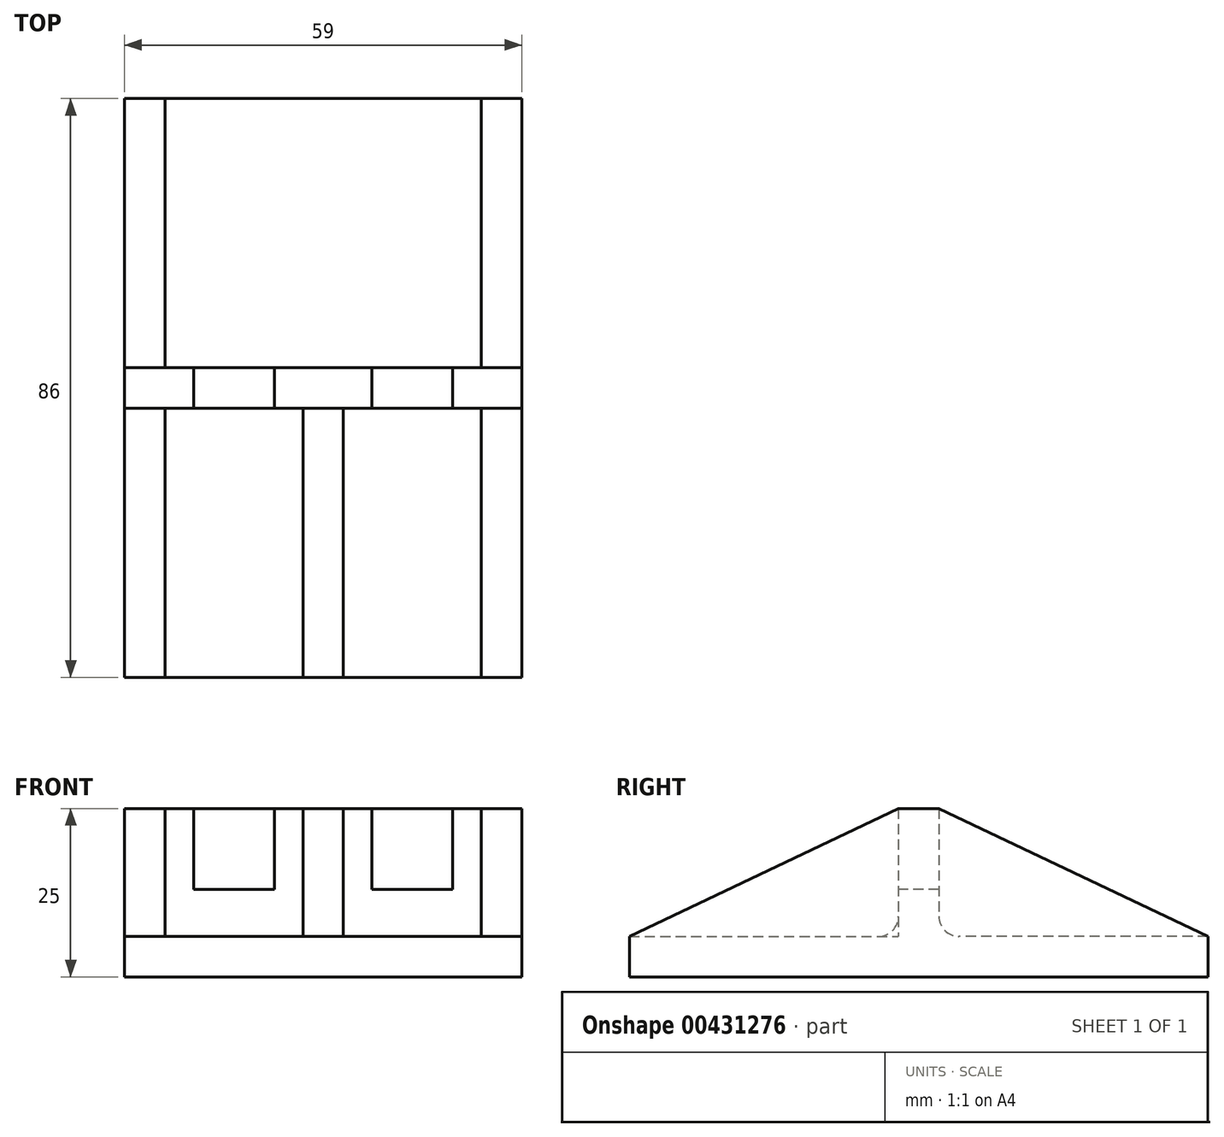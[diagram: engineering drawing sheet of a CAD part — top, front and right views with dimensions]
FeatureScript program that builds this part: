
annotation { "Feature Type Name" : "Feature", "Feature Type Description" : "" }
export const myFeature = defineFeature(function(context is Context, id is Id, definition is map)
    precondition{}
    {
        {
            var Q0;
            Q0=qCreatedBy(makeId("Top.planeOp"),FACE);
            var sketch = newSketch(context, id + "F0", { "sketchPlane" : qUnion([Q0])});
            skLineSegment(sketch, "E0.bottom", {"start": v(-29.5, 43) * mm, "end": v(29.5, 43) * mm});
            skLineSegment(sketch, "E0.top", {"start": v(-29.5, -43) * mm, "end": v(29.5, -43) * mm});
            skLineSegment(sketch, "E0.left", {"start": v(-29.5, 43) * mm, "end": v(-29.5, -43) * mm});
            skLineSegment(sketch, "E0.right", {"start": v(29.5, 43) * mm, "end": v(29.5, -43) * mm});
            skSolve(sketch);
        }
        {
            var Q0;
            Q0=makeQuery(id+"F0.imprint","IMPRINT",FACE,{"disambiguationData":[TD([[makeQuery(id+"F0.imprint","IMPRINT",EDGE,{"derivedFrom":sQuery(id+"F0.wireOp",EDGE,"E0.bottom")}),-1.0]])]});
            extrude(context, id + "F1", {"entities" : qUnion([Q0]), "depth" : 6 * mm});
        }
        {
            var Q0;
            Q0=makeQuery(id+"F1.opExtrude","CAP_FACE",FACE,{"disambiguationData":[OSD([sQuery(id+"F0.wireOp",EDGE,"E0.bottom"),sQuery(id+"F0.wireOp",EDGE,"E0.top"),sQuery(id+"F0.wireOp",EDGE,"E0.left"),sQuery(id+"F0.wireOp",EDGE,"E0.right")])],"isStart":false});
            var sketch = newSketch(context, id + "F2", { "sketchPlane" : qUnion([Q0])});
            skLineSegment(sketch, "E1.bottom", {"start": v(-29.5, 43) * mm, "end": v(-23.5, 43) * mm});
            skLineSegment(sketch, "E1.left", {"start": v(-29.5, 43) * mm, "end": v(-29.5, -43) * mm});
            skLineSegment(sketch, "E1.right", {"start": v(-23.5, 43) * mm, "end": v(-23.5, 3) * mm});
            skLineSegment(sketch, "E2.bottom", {"start": v(-23.5, 3) * mm, "end": v(23.5, 3) * mm});
            skLineSegment(sketch, "E2.top", {"start": v(-23.5, -3) * mm, "end": v(-3, -3) * mm});
            skLineSegment(sketch, "E2.right", {"start": v(29.5, 43) * mm, "end": v(29.5, -43) * mm});
            skLineSegment(sketch, "E3.bottom", {"start": v(-29.5, -43) * mm, "end": v(-23.5, -43) * mm});
            skLineSegment(sketch, "E3.right", {"start": v(-23.5, -43) * mm, "end": v(-23.5, -3) * mm});
            skLineSegment(sketch, "E4.bottom", {"start": v(29.5, -43) * mm, "end": v(23.5, -43) * mm});
            skLineSegment(sketch, "E4.right", {"start": v(23.5, -43) * mm, "end": v(23.5, -3) * mm});
            skLineSegment(sketch, "E5.bottom", {"start": v(29.5, 43) * mm, "end": v(23.5, 43) * mm});
            skLineSegment(sketch, "E5.right", {"start": v(23.5, 43) * mm, "end": v(23.5, 3) * mm});
            skLineSegment(sketch, "E6.bottom", {"start": v(3, -43) * mm, "end": v(-3, -43) * mm});
            skLineSegment(sketch, "E6.left", {"start": v(3, -43) * mm, "end": v(3, -3) * mm});
            skLineSegment(sketch, "E6.right", {"start": v(-3, -43) * mm, "end": v(-3, -3) * mm});
            skLineSegment(sketch, "E7.trimOffspring", {"start": v(3, -3) * mm, "end": v(23.5, -3) * mm});
            skPoint(sketch, "E8.orphan", {"position": v(29.5, -3) * mm});
            skSolve(sketch);
        }
        {
            var Q0;
            Q0=makeQuery(id+"F2.imprint","IMPRINT",FACE,{"disambiguationData":[TD([[makeQuery(id+"F2.imprint","IMPRINT",EDGE,{"derivedFrom":sQuery(id+"F2.wireOp",EDGE,"E1.bottom")}),-1.0]])]});
            extrude(context, id + "F3", {"entities" : qUnion([Q0]), "operationType" : NewBodyOperationType.ADD, "depth" : 19 * mm});
        }
        {
            var Q0;
            Q0=makeQuery(id+"F3.boolean.opBoolean","MERGE",FACE,{"derivedFrom":[makeQuery(id+"F1.opExtrude","SWEPT_FACE",FACE,{"disambiguationData":[OSD([sQuery(id+"F0.wireOp",EDGE,"E0.right")])]}),makeQuery(id+"F3.opExtrude","SWEPT_FACE",FACE,{"disambiguationData":[OSD([sQuery(id+"F2.wireOp",EDGE,"E2.right")])]})]});
            var sketch = newSketch(context, id + "F4", { "sketchPlane" : qUnion([Q0])});
            skLineSegment(sketch, "E9", {"start": v(-43, 6) * mm, "end": v(-3, 25) * mm});
            skLineSegment(sketch, "E10", {"start": v(-3, 25) * mm, "end": v(-43, 25) * mm});
            skLineSegment(sketch, "E11", {"start": v(-43, 25) * mm, "end": v(-43, 6) * mm});
            skLineSegment(sketch, "E12", {"start": v(43, 6) * mm, "end": v(3, 25) * mm});
            skLineSegment(sketch, "E13", {"start": v(3, 25) * mm, "end": v(43, 25) * mm});
            skLineSegment(sketch, "E14", {"start": v(43, 25) * mm, "end": v(43, 6) * mm});
            skSolve(sketch);
        }
        {
            var Q0;
            Q0=makeQuery(id+"F4.imprint","IMPRINT",FACE,{"disambiguationData":[TD([[makeQuery(id+"F4.imprint","IMPRINT",EDGE,{"derivedFrom":sQuery(id+"F4.wireOp",EDGE,"E9")}),1.0]])]});
            var Q1;
            Q1=makeQuery(id+"F4.imprint","IMPRINT",FACE,{"disambiguationData":[TD([[makeQuery(id+"F4.imprint","IMPRINT",EDGE,{"derivedFrom":sQuery(id+"F4.wireOp",EDGE,"E12")}),-1.0]])]});
            extrude(context, id + "F5", {"entities" : qUnion([Q0, Q1]), "operationType" : NewBodyOperationType.REMOVE, "endBound" : BoundingType.THROUGH_ALL, "oppositeDirection" : true, "depth" : 25 * mm});
        }
        {
            var Q0;
            Q0=makeQuery(id+"F3.opExtrude","SWEPT_FACE",FACE,{"disambiguationData":[OSD([sQuery(id+"F2.wireOp",EDGE,"E2.top")])]});
            var sketch = newSketch(context, id + "F6", { "sketchPlane" : qUnion([Q0])});
            skLineSegment(sketch, "E15.bottom", {"start": v(-19.25, 25) * mm, "end": v(-7.25, 25) * mm});
            skLineSegment(sketch, "E15.top", {"start": v(-19.25, 13) * mm, "end": v(-7.25, 13) * mm});
            skLineSegment(sketch, "E15.left", {"start": v(-19.25, 25) * mm, "end": v(-19.25, 13) * mm});
            skLineSegment(sketch, "E15.right", {"start": v(-7.25, 25) * mm, "end": v(-7.25, 13) * mm});
            skLineSegment(sketch, "E16.bottom", {"start": v(7.25, 25) * mm, "end": v(19.25, 25) * mm});
            skLineSegment(sketch, "E16.top", {"start": v(7.25, 13) * mm, "end": v(19.25, 13) * mm});
            skLineSegment(sketch, "E16.left", {"start": v(7.25, 25) * mm, "end": v(7.25, 13) * mm});
            skLineSegment(sketch, "E16.right", {"start": v(19.25, 25) * mm, "end": v(19.25, 13) * mm});
            skSolve(sketch);
        }
        {
            var Q0;
            Q0=makeQuery(id+"F6.imprint","IMPRINT",FACE,{"disambiguationData":[TD([[makeQuery(id+"F6.imprint","IMPRINT",EDGE,{"derivedFrom":sQuery(id+"F6.wireOp",EDGE,"E15.bottom")}),-1.0]])]});
            var Q1;
            Q1=makeQuery(id+"F6.imprint","IMPRINT",FACE,{"disambiguationData":[TD([[makeQuery(id+"F6.imprint","IMPRINT",EDGE,{"derivedFrom":sQuery(id+"F6.wireOp",EDGE,"E16.bottom")}),-1.0]])]});
            extrude(context, id + "F7", {"entities" : qUnion([Q0, Q1]), "oppositeDirection" : true, "depth" : 6 * mm});
        }
        {
            var Q0;
            Q0=makeQuery(id+"F3.opExtrude","CAP_EDGE",EDGE,{"disambiguationData":[OSD([sQuery(id+"F2.wireOp",EDGE,"E2.top")])],"isStart":true});
            var Q1;
            Q1=makeQuery(id+"F3.opExtrude","CAP_EDGE",EDGE,{"disambiguationData":[OSD([sQuery(id+"F2.wireOp",EDGE,"E7.trimOffspring")])],"isStart":true});
            var Q2;
            Q2=makeQuery(id+"F3.opExtrude","CAP_EDGE",EDGE,{"disambiguationData":[OSD([sQuery(id+"F2.wireOp",EDGE,"E2.bottom")])],"isStart":true});
            fillet(context, id + "F8", {"entities" : qUnion([Q0, Q1, Q2]), "radius" : 3 * mm, "tangentPropagation" : true, "allowEdgeOverflow" : false});
        }
    });
